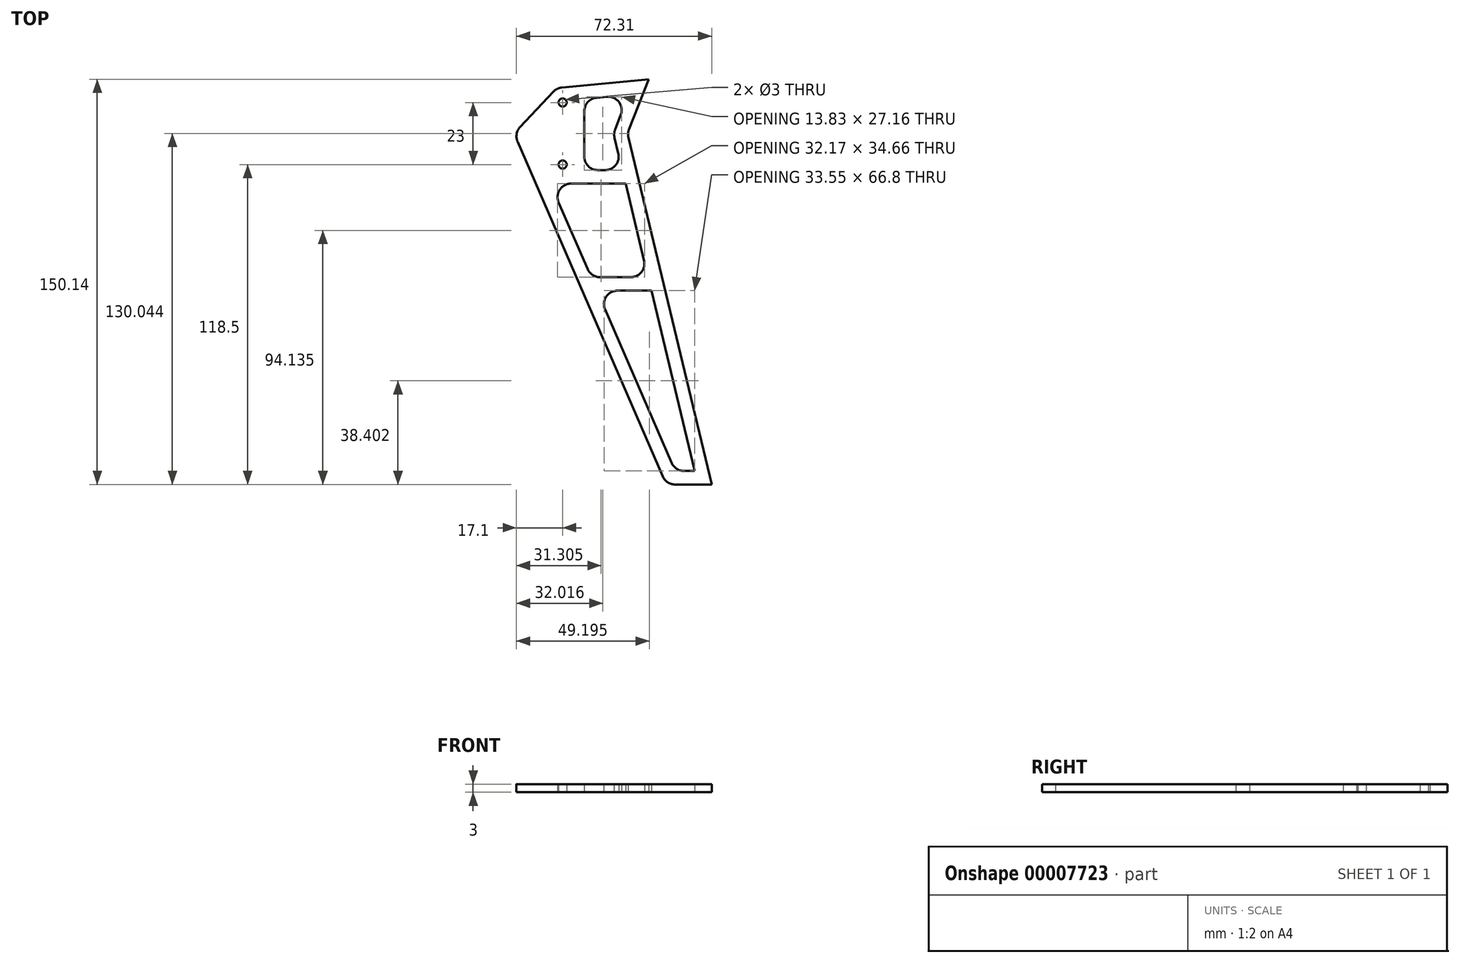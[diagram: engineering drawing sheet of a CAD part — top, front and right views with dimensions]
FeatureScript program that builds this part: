
annotation { "Feature Type Name" : "Feature", "Feature Type Description" : "" }
export const myFeature = defineFeature(function(context is Context, id is Id, definition is map)
    precondition{}
    {
        {
            var Q0;
            Q0=qCreatedBy(makeId("Top.planeOp"),FACE);
            var sketch = newSketch(context, id + "F0", { "sketchPlane" : qUnion([Q0])});
            skLineSegment(sketch, "E0", {"start": v(-27.44, 15.48) * mm, "end": v(-39.75, 2.4) * mm});
            skLineSegment(sketch, "E1", {"start": v(-40.7, -3.02) * mm, "end": v(13.06, -126.99) * mm});
            skLineSegment(sketch, "E2", {"start": v(17.65, -130) * mm, "end": v(31.21, -130) * mm});
            skLineSegment(sketch, "E3", {"start": v(31.21, -130) * mm, "end": v(0.37, -1.52) * mm});
            skLineSegment(sketch, "E4", {"start": v(0.57, 1.46) * mm, "end": v(7.87, 20.14) * mm});
            skLineSegment(sketch, "E5", {"start": v(7.87, 20.14) * mm, "end": v(-24.28, 17.03) * mm});
            skLineSegment(sketch, "E6", {"start": v(-24, -11.5) * mm, "end": v(-24, 0) * mm});
            skLineSegment(sketch, "E7", {"start": v(-24, 0) * mm, "end": v(-24, 11.5) * mm});
            skCircle(sketch, "E8", {"center": v(-24, 11.5) * mm, "radius": 1.5 * mm});
            skCircle(sketch, "E9", {"center": v(-24, -11.5) * mm, "radius": 1.5 * mm});
            skPoint(sketch, "E10.visualSharp", {"position": v(-42, 0) * mm});
            skArc(sketch, "E10.filletArc", {"start": v(-39.75, 2.4) * mm, "mid": v(-41.03, -0.17) * mm, "end": v(-40.7, -3.02) * mm});
            skPoint(sketch, "E11.visualSharp", {"position": v(-26.16, 16.85) * mm});
            skArc(sketch, "E11.filletArc", {"start": v(-24.28, 17.03) * mm, "mid": v(-26, 16.54) * mm, "end": v(-27.44, 15.48) * mm});
            skPoint(sketch, "E12.visualSharp", {"position": v(0, 0) * mm});
            skArc(sketch, "E12.filletArc", {"start": v(0.57, 1.46) * mm, "mid": v(0.24, -0.02) * mm, "end": v(0.37, -1.52) * mm});
            skPoint(sketch, "E13.visualSharp", {"position": v(14.37, -130) * mm});
            skArc(sketch, "E13.filletArc", {"start": v(13.06, -126.99) * mm, "mid": v(14.9, -129.18) * mm, "end": v(17.65, -130) * mm});
            skSolve(sketch);
        }
        {
            var Q0;
            Q0=makeQuery(id+"F0.imprint","IMPRINT",FACE,{"disambiguationData":[TD([[makeQuery(id+"F0.imprint","IMPRINT",EDGE,{"derivedFrom":sQuery(id+"F0.wireOp",EDGE,"E0")}),1.0]])]});
            var sketch = newSketch(context, id + "F1", { "sketchPlane" : qUnion([Q0])});
            skLineSegment(sketch, "E14", {"start": v(-20.9, -18.53) * mm, "end": v(-0.7, -18.53) * mm});
            skLineSegment(sketch, "E15", {"start": v(-0.7, -18.53) * mm, "end": v(6.15, -47.03) * mm});
            skLineSegment(sketch, "E16", {"start": v(1.29, -53.2) * mm, "end": v(-10.2, -53.2) * mm});
            skLineSegment(sketch, "E17", {"start": v(-14.8, -50.18) * mm, "end": v(-25.48, -25.52) * mm});
            skLineSegment(sketch, "E18", {"start": v(-0.7, -18.53) * mm, "end": v(-0.7, -18.53) * mm});
            skLineSegment(sketch, "E19", {"start": v(-3.7, -58.2) * mm, "end": v(4.89, -58.2) * mm});
            skLineSegment(sketch, "E20", {"start": v(9.75, -62.03) * mm, "end": v(24.87, -125) * mm});
            skLineSegment(sketch, "E21", {"start": v(24.87, -125) * mm, "end": v(20.93, -125) * mm});
            skLineSegment(sketch, "E22", {"start": v(16.34, -121.99) * mm, "end": v(-8.29, -65.18) * mm});
            skLineSegment(sketch, "E23", {"start": v(-16, 0) * mm, "end": v(-16, -8.53) * mm});
            skLineSegment(sketch, "E24", {"start": v(-11, -13.53) * mm, "end": v(-8.24, -13.53) * mm});
            skLineSegment(sketch, "E25", {"start": v(-3.37, -7.37) * mm, "end": v(-4.78, -1.52) * mm});
            skLineSegment(sketch, "E26", {"start": v(-4.57, 1.46) * mm, "end": v(-2.48, 6.83) * mm});
            skLineSegment(sketch, "E27", {"start": v(-7.62, 13.62) * mm, "end": v(-11.48, 13.25) * mm});
            skLineSegment(sketch, "E28", {"start": v(-16, 8.27) * mm, "end": v(-16, 0) * mm});
            skPoint(sketch, "E29.visualSharp", {"position": v(17.65, -125) * mm});
            skArc(sketch, "E29.filletArc", {"start": v(16.34, -121.99) * mm, "mid": v(18.19, -124.18) * mm, "end": v(20.93, -125) * mm});
            skPoint(sketch, "E30.visualSharp", {"position": v(8.83, -58.2) * mm});
            skPoint(sketch, "E31.visualSharp", {"position": v(-11.32, -58.2) * mm});
            skArc(sketch, "E31.filletArc", {"start": v(-3.7, -58.2) * mm, "mid": v(-7.88, -60.45) * mm, "end": v(-8.29, -65.18) * mm});
            skPoint(sketch, "E32.visualSharp", {"position": v(-13.49, -53.2) * mm});
            skArc(sketch, "E32.filletArc", {"start": v(-14.8, -50.18) * mm, "mid": v(-12.95, -52.38) * mm, "end": v(-10.2, -53.2) * mm});
            skPoint(sketch, "E33.visualSharp", {"position": v(7.63, -53.2) * mm});
            skArc(sketch, "E33.filletArc", {"start": v(1.29, -53.2) * mm, "mid": v(5.21, -51.3) * mm, "end": v(6.15, -47.03) * mm});
            skPoint(sketch, "E34.visualSharp", {"position": v(-28.51, -18.53) * mm});
            skArc(sketch, "E34.filletArc", {"start": v(-20.9, -18.53) * mm, "mid": v(-25.08, -20.8) * mm, "end": v(-25.48, -25.52) * mm});
            skPoint(sketch, "E35.visualSharp", {"position": v(-1.9, -13.53) * mm});
            skArc(sketch, "E35.filletArc", {"start": v(-8.24, -13.53) * mm, "mid": v(-4.3, -11.63) * mm, "end": v(-3.37, -7.37) * mm});
            skPoint(sketch, "E36.visualSharp", {"position": v(-16, -13.53) * mm});
            skArc(sketch, "E36.filletArc", {"start": v(-16, -8.53) * mm, "mid": v(-14.54, -12.07) * mm, "end": v(-11, -13.53) * mm});
            skPoint(sketch, "E37.visualSharp", {"position": v(-16, 12.81) * mm});
            skArc(sketch, "E37.filletArc", {"start": v(-11.48, 13.25) * mm, "mid": v(-14.7, 11.63) * mm, "end": v(-16, 8.27) * mm});
            skPoint(sketch, "E38.visualSharp", {"position": v(0.48, 14.4) * mm});
            skArc(sketch, "E38.filletArc", {"start": v(-2.48, 6.83) * mm, "mid": v(-3.15, 11.66) * mm, "end": v(-7.62, 13.62) * mm});
            skLineSegment(sketch, "E39", {"start": v(8.83, -58.2) * mm, "end": v(4.89, -58.2) * mm});
            skLineSegment(sketch, "E40", {"start": v(9.75, -62.03) * mm, "end": v(8.83, -58.2) * mm});
            skPoint(sketch, "E41.visualSharp", {"position": v(-5.14, 0) * mm});
            skArc(sketch, "E41.filletArc", {"start": v(-4.57, 1.46) * mm, "mid": v(-4.9, -0.02) * mm, "end": v(-4.78, -1.52) * mm});
            skSolve(sketch);
        }
        {
            var Q0;
            Q0=makeQuery(id+"F0.imprint","IMPRINT",FACE,{"disambiguationData":[TD([[makeQuery(id+"F0.imprint","IMPRINT",EDGE,{"derivedFrom":sQuery(id+"F0.wireOp",EDGE,"E0")}),1.0]])]});
            extrude(context, id + "F2", {"entities" : qUnion([Q0]), "depth" : 3 * mm});
        }
        {
            var Q0;
            Q0 = qSketchRegion(id + "F1", true);
            extrude(context, id + "F3", {"entities" : qUnion([Q0]), "operationType" : NewBodyOperationType.REMOVE, "depth" : 25 * mm});
        }
    });
